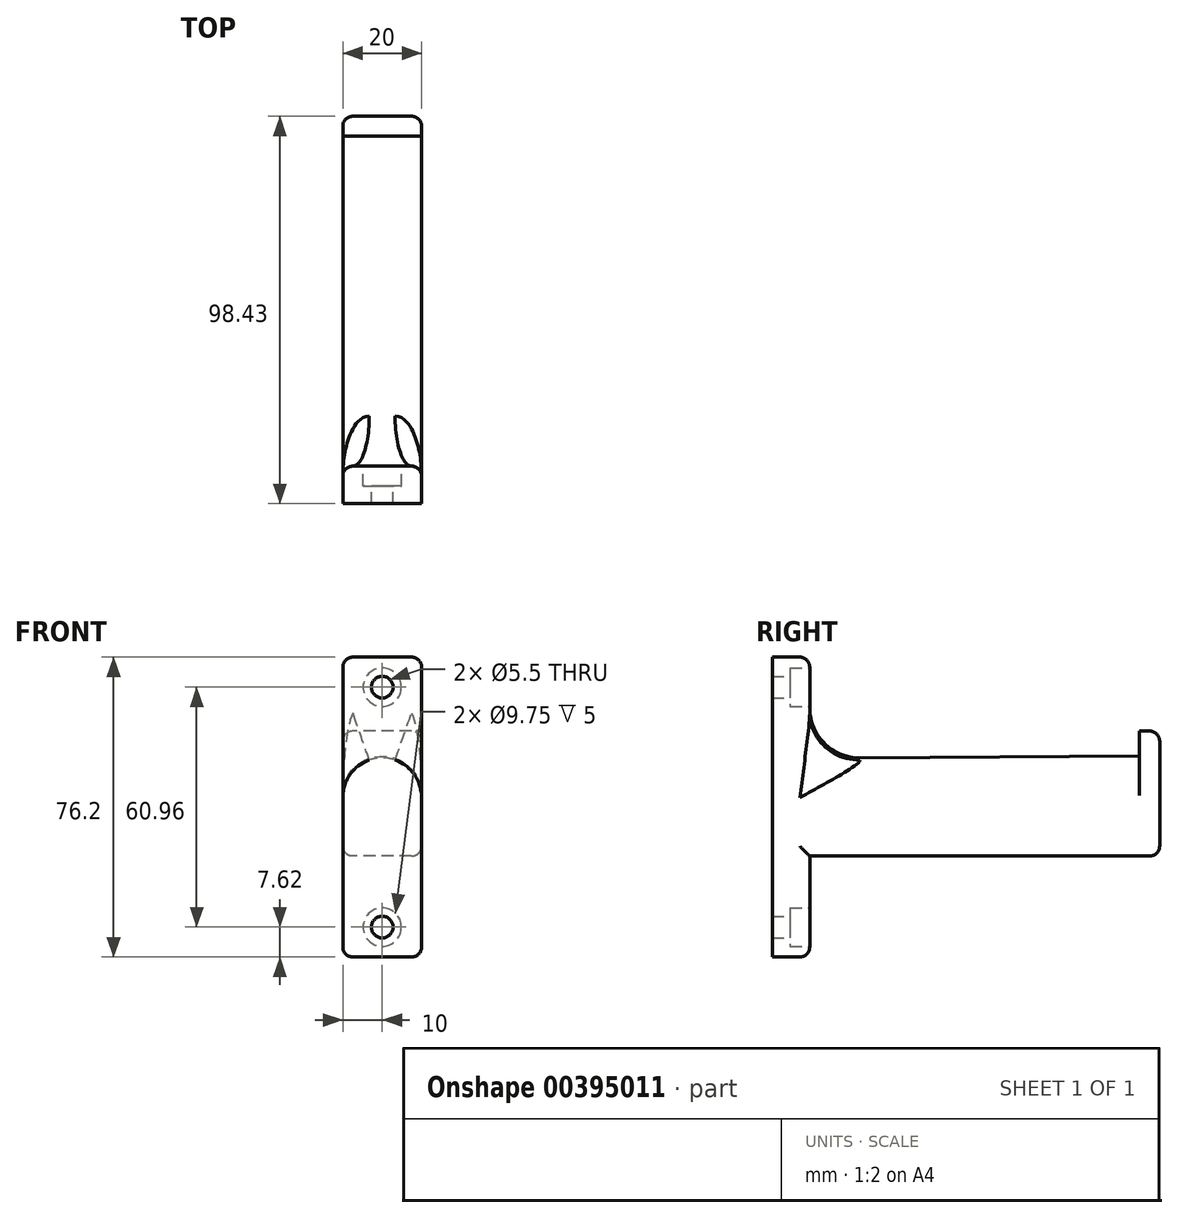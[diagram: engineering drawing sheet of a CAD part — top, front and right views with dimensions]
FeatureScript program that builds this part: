
annotation { "Feature Type Name" : "Feature", "Feature Type Description" : "" }
export const myFeature = defineFeature(function(context is Context, id is Id, definition is map)
    precondition{}
    {
        {
            var Q0;
            Q0=qCreatedBy(makeId("Right.planeOp"),FACE);
            var sketch = newSketch(context, id + "F0", { "sketchPlane" : qUnion([Q0])});
            skLineSegment(sketch, "E0", {"start": v(88.9, 19.3) * mm, "end": v(88.9, -12.44) * mm});
            skLineSegment(sketch, "E1", {"start": v(88.9, -12.44) * mm, "end": v(0, -12.44) * mm});
            skLineSegment(sketch, "E2", {"start": v(88.9, 19.3) * mm, "end": v(83.82, 19.3) * mm});
            skLineSegment(sketch, "E3", {"start": v(83.82, 19.3) * mm, "end": v(83.82, 12.96) * mm});
            skLineSegment(sketch, "E4", {"start": v(83.82, 12.96) * mm, "end": v(0, 12.44) * mm});
            skLineSegment(sketch, "E5", {"start": v(0, -12.44) * mm, "end": v(0, 12.44) * mm});
            skPoint(sketch, "E6", {"position": v(0, 0) * mm});
            skLineSegment(sketch, "E7.bottom", {"start": v(0, 38.1) * mm, "end": v(-9.53, 38.1) * mm});
            skLineSegment(sketch, "E7.top", {"start": v(0, -38.1) * mm, "end": v(-9.53, -38.1) * mm});
            skLineSegment(sketch, "E7.left", {"start": v(0, 38.1) * mm, "end": v(0, -38.1) * mm});
            skLineSegment(sketch, "E7.right", {"start": v(-9.53, 38.1) * mm, "end": v(-9.52, -38.1) * mm});
            skSolve(sketch);
        }
        {
            var Q0;
            Q0=makeQuery(id+"F0.imprint","IMPRINT",FACE,{"disambiguationData":[TD([[makeQuery(id+"F0.imprint","IMPRINT",EDGE,{"derivedFrom":sQuery(id+"F0.wireOp",EDGE,"ZzaRVxnF-bxBg-v67o-X8qs-SqVxovf9bs2E.top")}),-1.0]])]});
            var Q1;
            Q1=makeQuery(id+"F0.imprint","IMPRINT",FACE,{"disambiguationData":[TD([[makeQuery(id+"F0.imprint","IMPRINT",EDGE,{"derivedFrom":sQuery(id+"F0.wireOp",EDGE,"E0")}),-1.0]])]});
            var Q2;
            {var subQ3=sQuery(id+"F0.wireOp",EDGE,"E7.bottom");Q2=makeQuery(id+"F0.imprint","IMPRINT",FACE,{"disambiguationData":[TD([[makeQuery(id+"F0.imprint","IMPRINT",EDGE,{"derivedFrom":subQ3}),1.0]])]});}
            extrude(context, id + "F1", {"entities" : qUnion([Q0, Q1, Q2]), "depth" : 20 * mm, "offsetDistance" : 25.4 * mm});
        }
        {
            var Q0;
            Q0=makeQuery(id+"F1.opExtrude","CAP_EDGE",EDGE,{"disambiguationData":[OSD([sQuery(id+"F0.wireOp",EDGE,"E4")])],"isStart":false});
            var Q1;
            Q1=makeQuery(id+"F1.opExtrude","CAP_EDGE",EDGE,{"disambiguationData":[OSD([sQuery(id+"F0.wireOp",EDGE,"E4")])],"isStart":true});
            fillet(context, id + "F2", {"entities" : qUnion([Q0, Q1]), "radius" : 10 * mm, "tangentPropagation" : true, "allowEdgeOverflow" : false});
        }
        {
            var Q0;
            Q0=makeQuery(id+"F1.opExtrude","CAP_EDGE",EDGE,{"disambiguationData":[OSD([sQuery(id+"F0.wireOp",EDGE,"E7.bottom")])],"isStart":false});
            var Q1;
            {var subQ0=sQuery(id+"F0.wireOp",EDGE,"E7.left");Q1=makeQuery(id+"F1.opExtrude","CAP_EDGE",EDGE,{"disambiguationData":[OSD([subQ0]),TDD([makeQuery(id+"F0.imprint","IMPRINT",EDGE,{"disambiguationData":[TD([[makeQuery(id+"F0.imprint","INTERSECT",VERTEX,{"derivedFrom":[sQuery(id+"F0.wireOp",EDGE,"E4"),subQ0]}),1.0]])],"derivedFrom":subQ0})])],"isStart":false});}
            var Q2;
            Q2=makeQuery(id+"F1.opExtrude","CAP_EDGE",EDGE,{"disambiguationData":[OSD([sQuery(id+"F0.wireOp",EDGE,"E2")])],"isStart":false});
            var Q3;
            Q3=makeQuery(id+"F1.opExtrude","CAP_EDGE",EDGE,{"disambiguationData":[OSD([sQuery(id+"F0.wireOp",EDGE,"E2")])],"isStart":true});
            var Q4;
            Q4=makeQuery(id+"F1.opExtrude","CAP_EDGE",EDGE,{"disambiguationData":[OSD([sQuery(id+"F0.wireOp",EDGE,"E1")])],"isStart":false});
            var Q5;
            Q5=makeQuery(id+"F1.opExtrude","CAP_EDGE",EDGE,{"disambiguationData":[OSD([sQuery(id+"F0.wireOp",EDGE,"E1")])],"isStart":true});
            var Q6;
            Q6=makeQuery(id+"F1.opExtrude","CAP_EDGE",EDGE,{"disambiguationData":[OSD([sQuery(id+"F0.wireOp",EDGE,"E0")])],"isStart":false});
            var Q7;
            Q7=makeQuery(id+"F1.opExtrude","CAP_EDGE",EDGE,{"disambiguationData":[OSD([sQuery(id+"F0.wireOp",EDGE,"E0")])],"isStart":true});
            var Q8;
            Q8=makeQuery(id+"F1.opExtrude","SWEPT_EDGE",EDGE,{"disambiguationData":[OSD([sQuery(id+"F0.wireOp",EDGE,"E0"),sQuery(id+"F0.wireOp",EDGE,"E1")])]});
            var Q9;
            Q9=makeQuery(id+"F1.opExtrude","SWEPT_EDGE",EDGE,{"disambiguationData":[OSD([sQuery(id+"F0.wireOp",EDGE,"E0"),sQuery(id+"F0.wireOp",EDGE,"E2")])]});
            var Q10;
            {var subQ0=sQuery(id+"F0.wireOp",EDGE,"E7.left");Q10=makeQuery(id+"F1.opExtrude","CAP_EDGE",EDGE,{"disambiguationData":[OSD([subQ0]),TDD([makeQuery(id+"F0.imprint","IMPRINT",EDGE,{"disambiguationData":[TD([[makeQuery(id+"F0.imprint","INTERSECT",VERTEX,{"derivedFrom":[sQuery(id+"F0.wireOp",EDGE,"E4"),subQ0]}),1.0]])],"derivedFrom":subQ0})])],"isStart":true});}
            var Q11;
            Q11=makeQuery(id+"F1.opExtrude","CAP_EDGE",EDGE,{"disambiguationData":[OSD([sQuery(id+"F0.wireOp",EDGE,"E7.bottom")])],"isStart":true});
            var Q12;
            {var subQ0=sQuery(id+"F0.wireOp",EDGE,"E7.left");Q12=makeQuery(id+"F1.opExtrude","CAP_EDGE",EDGE,{"disambiguationData":[OSD([subQ0]),TDD([makeQuery(id+"F0.imprint","IMPRINT",EDGE,{"disambiguationData":[TD([[makeQuery(id+"F0.imprint","INTERSECT",VERTEX,{"derivedFrom":[sQuery(id+"F0.wireOp",EDGE,"E1"),subQ0]}),-1.0]])],"derivedFrom":subQ0})])],"isStart":true});}
            var Q13;
            {var subQ0=sQuery(id+"F0.wireOp",EDGE,"E7.left");Q13=makeQuery(id+"F1.opExtrude","CAP_EDGE",EDGE,{"disambiguationData":[OSD([subQ0]),TDD([makeQuery(id+"F0.imprint","IMPRINT",EDGE,{"disambiguationData":[TD([[makeQuery(id+"F0.imprint","INTERSECT",VERTEX,{"derivedFrom":[sQuery(id+"F0.wireOp",EDGE,"E1"),subQ0]}),-1.0]])],"derivedFrom":subQ0})])],"isStart":false});}
            var Q14;
            Q14=makeQuery(id+"F1.opExtrude","CAP_EDGE",EDGE,{"disambiguationData":[OSD([sQuery(id+"F0.wireOp",EDGE,"E7.top")])],"isStart":true});
            var Q15;
            Q15=makeQuery(id+"F1.opExtrude","SWEPT_EDGE",EDGE,{"disambiguationData":[OSD([sQuery(id+"F0.wireOp",EDGE,"E7.top"),sQuery(id+"F0.wireOp",EDGE,"E7.left")])]});
            var Q16;
            Q16=makeQuery(id+"F1.opExtrude","CAP_EDGE",EDGE,{"disambiguationData":[OSD([sQuery(id+"F0.wireOp",EDGE,"E7.top")])],"isStart":false});
            var Q17;
            Q17=makeQuery(id+"F1.opExtrude","SWEPT_EDGE",EDGE,{"disambiguationData":[OSD([sQuery(id+"F0.wireOp",EDGE,"E7.bottom"),sQuery(id+"F0.wireOp",EDGE,"E7.left")])]});
            fillet(context, id + "F3", {"entities" : qUnion([Q0, Q1, Q2, Q3, Q4, Q5, Q6, Q7, Q8, Q9, Q10, Q11, Q12, Q13, Q14, Q15, Q16, Q17]), "radius" : 2.54 * mm, "tangentPropagation" : true, "allowEdgeOverflow" : false});
        }
        {
            var Q0;
            Q0=makeQuery(id+"F1.opExtrude","SWEPT_EDGE",EDGE,{"disambiguationData":[OSD([sQuery(id+"F0.wireOp",EDGE,"E1"),sQuery(id+"F0.wireOp",EDGE,"lfqeIMb6-H9NB-MlbH-iFgg-f0orbcGI41XN")])]});
            var Q1;
            {var subQ0=sQuery(id+"F0.wireOp",EDGE,"E7.left");var subQ1=sQuery(id+"F0.wireOp",EDGE,"E4");Q1=makeQuery(id+"F2.opFillet","BLEND_EDGE",EDGE,{"blendedFrom":[makeQuery(id+"F1.opExtrude","CAP_EDGE",EDGE,{"disambiguationData":[OSD([subQ1])],"isStart":true}),makeQuery(id+"F1.opExtrude","SWEPT_FACE",FACE,{"disambiguationData":[OSD([subQ0]),TDD([makeQuery(id+"F0.imprint","IMPRINT",EDGE,{"disambiguationData":[TD([[makeQuery(id+"F0.imprint","INTERSECT",VERTEX,{"derivedFrom":[subQ1,subQ0]}),1.0]])],"derivedFrom":subQ0})])]})],"blendedInto":[makeQuery(id+"F1.opExtrude","SWEPT_FACE",FACE,{"disambiguationData":[OSD([subQ0]),TDD([makeQuery(id+"F0.imprint","IMPRINT",EDGE,{"disambiguationData":[TD([[makeQuery(id+"F0.imprint","INTERSECT",VERTEX,{"derivedFrom":[subQ1,subQ0]}),1.0]])],"derivedFrom":subQ0})])]})]});}
            fillet(context, id + "F4", {"entities" : qUnion([Q0, Q1]), "radius" : 12.7 * mm, "tangentPropagation" : true, "allowEdgeOverflow" : false});
        }
        {
            var Q0;
            {var subQ0=sQuery(id+"F0.wireOp",EDGE,"E7.left");Q0=makeQuery(id+"F1.opExtrude","SWEPT_FACE",FACE,{"disambiguationData":[OSD([subQ0]),TDD([makeQuery(id+"F0.imprint","IMPRINT",EDGE,{"disambiguationData":[TD([[makeQuery(id+"F0.imprint","INTERSECT",VERTEX,{"derivedFrom":[sQuery(id+"F0.wireOp",EDGE,"E4"),subQ0]}),1.0]])],"derivedFrom":subQ0})])]});}
            var sketch = newSketch(context, id + "F5", { "sketchPlane" : qUnion([Q0])});
            skPoint(sketch, "E8", {"position": v(-10, 30.48) * mm});
            skPoint(sketch, "E8.positionSnap0", {"position": v(-10, 35.56) * mm});
            skPoint(sketch, "E9", {"position": v(-10, -30.48) * mm});
            skPoint(sketch, "E9.positionSnap0", {"position": v(-10, 25.22) * mm});
            skSolve(sketch);
        }
        {
            var Q0;
            Q0=sQuery(id+"F5.wireOp",VERTEX,"E8");
            var Q1;
            Q1=sQuery(id+"F5.wireOp",VERTEX,"E9");
            var Q2;
            Q2=makeQuery(id+"F1.opExtrude","SWEPT_BODY",BODY,{"disambiguationData":[OSD([sQuery(id+"F0.wireOp",EDGE,"E0"),sQuery(id+"F0.wireOp",EDGE,"E1"),sQuery(id+"F0.wireOp",EDGE,"E2"),sQuery(id+"F0.wireOp",EDGE,"E3"),sQuery(id+"F0.wireOp",EDGE,"E4"),sQuery(id+"F0.wireOp",EDGE,"E7.bottom"),sQuery(id+"F0.wireOp",EDGE,"E7.top"),sQuery(id+"F0.wireOp",EDGE,"E7.left"),sQuery(id+"F0.wireOp",EDGE,"E7.right")])]});
            hole(context, id + "F6", {"style" : HoleStyle.C_BORE, "endStyle" : HoleEndStyle.THROUGH, "standardTappedOrClearance" : lookupTablePath({ "standard" : "ISO", "fit" : "Normal", "size" : "M5", "type" : "Clearance" }), "standardBlindInLast" : lookupTablePath({ "fit" : "Standard", "standard" : "ISO", "size" : "M5", "type" : "Clearance" }), "holeDiameter" : 5.5 * mm, "cBoreDiameter" : 9.75 * mm, "cBoreDepth" : 5 * mm, "majorDiameter" : 6.35 * mm, "isTappedThrough" : true, "tappedDepth" : 5.6 * mm, "tapClearance" : 0, "startFromSketch" : true, "locations" : qUnion([Q0, Q1]), "scope" : qUnion([Q2])});
        }
    });
